# Revit family: Diffuser-Carnes-SFPA-Fixed-Surface-or-T_Bar
name_source: partatom
category: Duct Accessories
revit_build: Autodesk Revit Architecture 2012 (Build: 20110309_2315(x64)
units: mm (PartAtom-declared; Revit-internal decimal feet)

## types (8) — shared parameters
Baffle Option = http://www.carnes.com
Catalog = http://www.carnes.com
Default Elevation = 0"
Description = Square Stamped Plaque Diffusers
Diameter = 6"
Doon Fineline = http://www.carnes.com
Field Balancing = http://www.carnes.com
Flow = 0 CFM
Inner Diameter C = 6"
Manufacturer = CARNES COMPANY
Model = SFPA
Product Page URL = http://www.carnes.com
Radius = 3"
Specification Sheet = http://www.carnes.com
Subcatagory = Air Distribution
Supply Connection = Diffuser Supply Connector
Supply Connector = Yes
URL = http://www.carnes.com
Unit = Metal - Carnes - Steel Galvanized

## per-type parameters (varying)
| type | Depth B | Diffuser Height F | Inner Plate Cover D | Overall Height E | Width A |
| SFPA 11x6 | 11 3/4" | 3" | 9" | 3 7/16" | 11 3/4" |
| SFPA 11x8 | 11 3/4" | 3" | 9" | 3 7/16" | 11 3/4" |
| SFPA 24x6 | 23 3/4" | 3 1/2" | 17 5/8" | 3 7/8" | 23 3/4" |
| SFPA 24x8 | 23 3/4" | 3 1/2" | 17 5/8" | 3 7/8" | 23 3/4" |
| SFPA 24x10 | 23 3/4" | 3 1/2" | 17 5/8" | 3 7/8" | 23 3/4" |
| SFPA 24x12 | 23 3/4" | 3 1/2" | 17 5/8" | 3 7/8" | 23 3/4" |
| SFPA 24x14 | 23 3/4" | 3 1/2" | 17 5/8" | 3 7/8" | 23 3/4" |
| SFPA 24x16 | 23 3/4" | 3 1/2" | 17 5/8" | 3 7/8" | 23 3/4" |

## geometry (parser evidence)
native form markers: Blend x3, Sweep x5
no freeform markers — native parametric forms only
